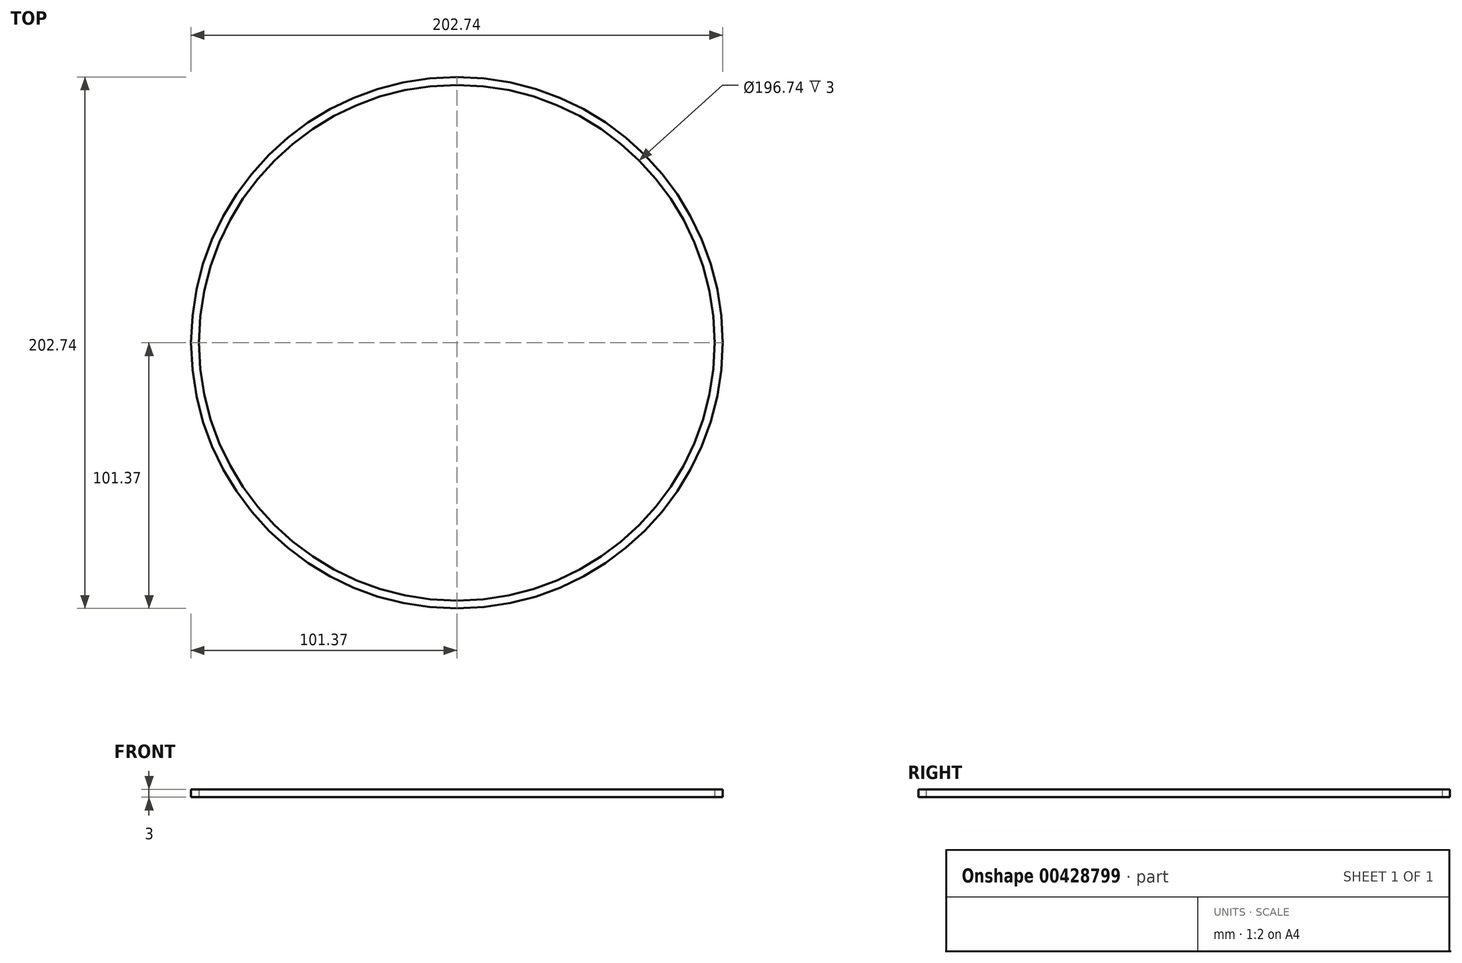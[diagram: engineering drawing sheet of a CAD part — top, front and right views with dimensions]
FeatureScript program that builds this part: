
annotation { "Feature Type Name" : "Feature", "Feature Type Description" : "" }
export const myFeature = defineFeature(function(context is Context, id is Id, definition is map)
    precondition{}
    {
        {
            var Q0;
            Q0=qCreatedBy(makeId("Top.planeOp"),FACE);
            var sketch = newSketch(context, id + "F0", { "sketchPlane" : qUnion([Q0])});
            skCircle(sketch, "E0", {"center": v(0, 0) * mm, "radius": 101.37 * mm});
            skCircle(sketch, "E1", {"center": v(0, 0) * mm, "radius": 98.37 * mm});
            skSolve(sketch);
        }
        {
            var Q0;
            Q0=makeQuery(id+"F0.imprint","IMPRINT",FACE,{"disambiguationData":[TD([[makeQuery(id+"F0.imprint","IMPRINT",EDGE,{"derivedFrom":sQuery(id+"F0.wireOp",EDGE,"E0")}),1.0]])]});
            extrude(context, id + "F1", {"entities" : qUnion([Q0]), "depth" : 3 * mm});
        }
    });
